# Revit family: Towel dispenser_CWS_Heavy duty
name_source: partatom
category: Plumbing Fixtures
revit_build: Autodesk Revit Architecture 2014 (Build: 20130308_1515(x64)
units: mm (PartAtom-declared; Revit-internal decimal feet)

## types (1)
- Plastic - IL_Heavy_Duty - CWS
    BIMobject category = Dispensers
    Date of publishing = 2015-09-17
    Deapth = 259 mm  [stored 0.849738 ft]
    Description = Heavy Duty cotton towel dispenser for a cotton towel roll measuring 40 × 0.27 m with 30 cm towel feed. Plastic gears with automatic dosing and uncoupling systems and backstop. White-red fill-level display on the front. Housing made of impact-proof, anti-static plastic, with lock. Rounded edges ensure no risk of injury. Comes complete with fastening materials, delivery and installation, without cotton towel roll (available to rent on subscription).

Dispenser:
Heavy Duty: 102000

Cotton towel rolls:
Universal white: 151000, Universal blue: 152000
    Design country = Switzerland
    EAN code = 4049657003534
    Edition number = 1
    Height = 476 mm
    IFC Classification = Furniture
    Manufacturer country = Switzerland
    Manufacturer name = CWS-boco
    Manufacturer url = http://cws-boco.ie
    Material = Plastic - IL_Heavy_Duty - CWS
    NBS Reference Code = 31-76
    NBS Reference Description = Sanitary Dispensing And Disposal Units
    Nominal height = 476
    Nominal width = 387
    Product Guid = b46cc673-2084-4b95-b05e-c9a4dcd23b0c
    Product SKU = 102000
    Product certification = http://www.cws-boco.de
    Product data url = http://bimobject.com
    Product family = CWS IndustryLine
    Product group = Cotton towel dispenser
    QR code = http://bimobject.com
    UNSPSC Code = 301815
    UNSPSC name = Sanitary ware
    URL = http://cws-boco.ie
    Uniclass 1.4 Code = JN13
    Uniclass 1.4 Description = Sanitary appliances/fittings
    Uniclass 2.0 Code = PR-31-76
    Uniclass 2.0 Description = Sanitary Dispensing And Disposal Units
    Weight Net (Kg) = 7.4
    Width = 387 mm
    Youtube clip = https://www.youtube.com

note: [stored X ft] marks values corroborated as IEEE doubles in the binary element streams (Revit-internal decimal feet)

## geometry (parser evidence)
native form markers: Sweep x4
no freeform markers — native parametric forms only
